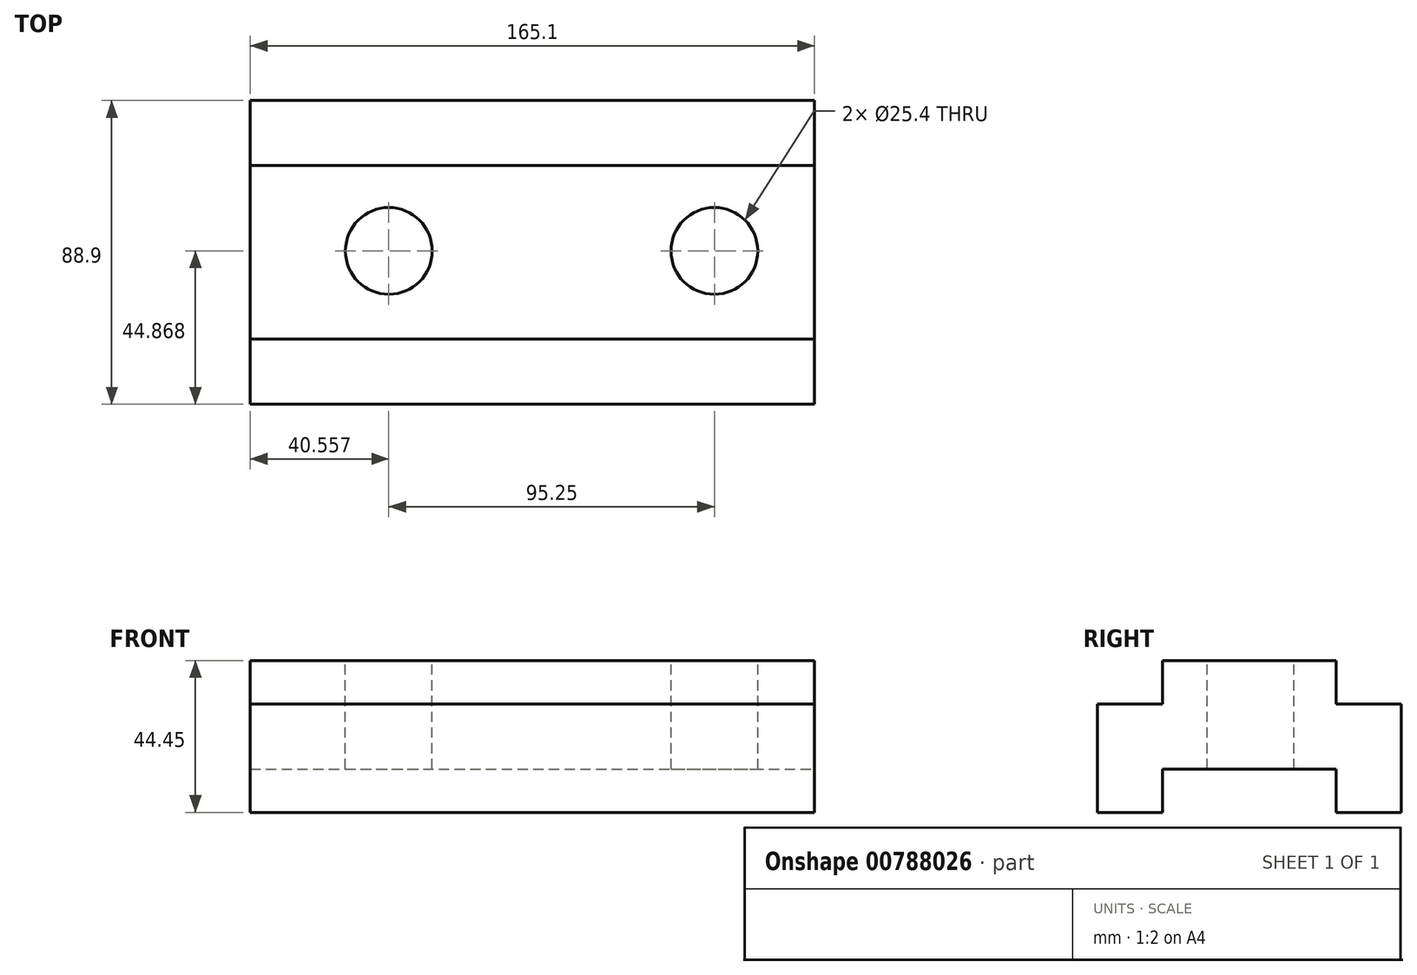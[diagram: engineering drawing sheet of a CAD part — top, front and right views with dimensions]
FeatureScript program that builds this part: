
annotation { "Feature Type Name" : "Feature", "Feature Type Description" : "" }
export const myFeature = defineFeature(function(context is Context, id is Id, definition is map)
    precondition{}
    {
        {
            var Q0;
            Q0=qCreatedBy(makeId("Right.planeOp"),FACE);
            var sketch = newSketch(context, id + "F0", { "sketchPlane" : qUnion([Q0])});
            skLineSegment(sketch, "E0", {"start": v(0, 0) * mm, "end": v(19.05, 0) * mm});
            skLineSegment(sketch, "E1", {"start": v(19.05, 0) * mm, "end": v(19.05, 12.7) * mm});
            skLineSegment(sketch, "E2", {"start": v(19.05, 12.7) * mm, "end": v(69.85, 12.7) * mm});
            skLineSegment(sketch, "E3", {"start": v(69.85, 12.7) * mm, "end": v(69.85, 0) * mm});
            skLineSegment(sketch, "E4", {"start": v(69.85, 0) * mm, "end": v(88.9, 0) * mm});
            skLineSegment(sketch, "E5", {"start": v(88.9, 0) * mm, "end": v(88.9, 31.75) * mm});
            skLineSegment(sketch, "E6", {"start": v(88.9, 31.75) * mm, "end": v(69.85, 31.75) * mm});
            skLineSegment(sketch, "E7", {"start": v(69.85, 31.75) * mm, "end": v(69.85, 44.45) * mm});
            skLineSegment(sketch, "E8", {"start": v(69.85, 44.45) * mm, "end": v(19.05, 44.45) * mm});
            skLineSegment(sketch, "E9", {"start": v(0, 0) * mm, "end": v(0, 31.75) * mm});
            skLineSegment(sketch, "E10", {"start": v(0, 31.75) * mm, "end": v(19.05, 31.75) * mm});
            skLineSegment(sketch, "E11", {"start": v(19.05, 31.75) * mm, "end": v(19.05, 44.45) * mm});
            skSolve(sketch);
        }
        {
            var Q0;
            Q0=makeQuery(id+"F0.imprint","IMPRINT",FACE,{"disambiguationData":[TD([[makeQuery(id+"F0.imprint","IMPRINT",EDGE,{"derivedFrom":sQuery(id+"F0.wireOp",EDGE,"E0")}),1.0]])]});
            extrude(context, id + "F1", {"entities" : qUnion([Q0]), "oppositeDirection" : true, "depth" : 165.1 * mm, "offsetDistance" : 25.4 * mm});
        }
        {
            var Q0;
            Q0=makeQuery(id+"F1.opExtrude","SWEPT_FACE",FACE,{"disambiguationData":[OSD([sQuery(id+"F0.wireOp",EDGE,"E8")])]});
            var sketch = newSketch(context, id + "F2", { "sketchPlane" : qUnion([Q0])});
            skLineSegment(sketch, "E12", {"start": v(-165.1, 44.45) * mm, "end": v(-123.83, 44.45) * mm, "construction": true});
            skSolve(sketch);
        }
        {
            var Q0;
            {var subQ0=sQuery(id+"F0.wireOp",EDGE,"E8");Q0=makeQuery(id+"F2.imprint","IMPRINT",FACE,{"disambiguationData":[TD([[makeQuery(id+"F2.imprint","IMPRINT",EDGE,{"derivedFrom":makeQuery(id+"F1.opExtrude","CAP_EDGE",EDGE,{"disambiguationData":[OSD([subQ0])],"isStart":true})}),-1.0]])]});}
            var sketch = newSketch(context, id + "F3", { "sketchPlane" : qUnion([Q0])});
            skLineSegment(sketch, "E13", {"start": v(-124.54, 44.87) * mm, "end": v(-29.3, 44.87) * mm, "construction": true});
            skCircle(sketch, "E14", {"center": v(-29.3, 44.87) * mm, "radius": 12.7 * mm});
            skCircle(sketch, "E15", {"center": v(-124.54, 44.87) * mm, "radius": 12.7 * mm});
            skSolve(sketch);
        }
        {
            var Q0;
            Q0 = qSketchRegion(id + "F3", true);
            extrude(context, id + "F4", {"entities" : qUnion([Q0]), "operationType" : NewBodyOperationType.REMOVE, "oppositeDirection" : true, "depth" : 101.6 * mm, "offsetDistance" : 25.4 * mm});
        }
    });
